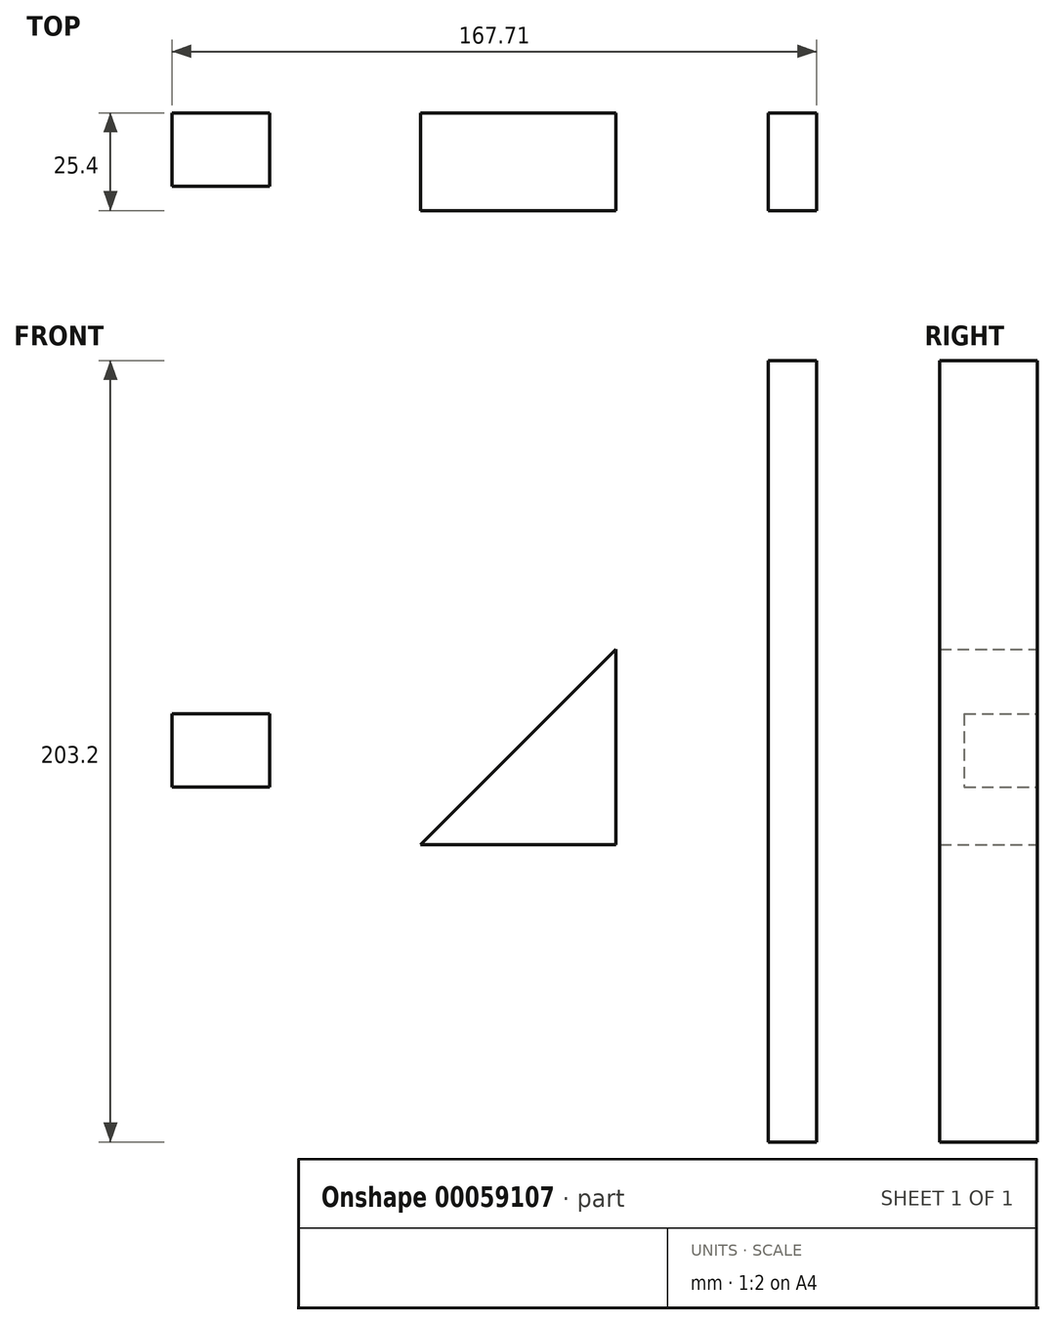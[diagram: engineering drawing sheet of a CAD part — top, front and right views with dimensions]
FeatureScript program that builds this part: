
annotation { "Feature Type Name" : "Feature", "Feature Type Description" : "" }
export const myFeature = defineFeature(function(context is Context, id is Id, definition is map)
    precondition{}
    {
        {
            var Q0;
            Q0=qCreatedBy(makeId("Front.planeOp"),FACE);
            var sketch = newSketch(context, id + "F0", { "sketchPlane" : qUnion([Q0])});
            skLineSegment(sketch, "E0.rect.bottom", {"start": v(6.35, -101.6) * mm, "end": v(-6.35, -101.6) * mm});
            skLineSegment(sketch, "E0.rect.top", {"start": v(6.35, 101.6) * mm, "end": v(-6.35, 101.6) * mm});
            skLineSegment(sketch, "E0.rect.left", {"start": v(6.35, -101.6) * mm, "end": v(6.35, 101.6) * mm});
            skLineSegment(sketch, "E0.rect.right", {"start": v(-6.35, -101.6) * mm, "end": v(-6.35, 101.6) * mm});
            skPoint(sketch, "E0.rect.middle", {"position": v(0, 0) * mm});
            skSolve(sketch);
        }
        {
            var Q0;
            Q0=makeQuery(id+"F0.imprint","IMPRINT",FACE,{"disambiguationData":[TD([[makeQuery(id+"F0.imprint","IMPRINT",EDGE,{"derivedFrom":sQuery(id+"F0.wireOp",EDGE,"E0.rect.bottom")}),-1.0]])]});
            extrude(context, id + "F1", {"entities" : qUnion([Q0]), "depth" : 25.4 * mm});
        }
        {
            var Q0;
            Q0=qCreatedBy(makeId("Front.planeOp"),FACE);
            var sketch = newSketch(context, id + "F2", { "sketchPlane" : qUnion([Q0])});
            skLineSegment(sketch, "E1.top", {"start": v(-96.76, -24.34) * mm, "end": v(-45.96, -24.34) * mm});
            skLineSegment(sketch, "E1.right", {"start": v(-45.96, 26.46) * mm, "end": v(-45.96, -24.34) * mm});
            skLineSegment(sketch, "E2", {"start": v(-96.76, -24.34) * mm, "end": v(-45.96, 26.46) * mm});
            skSolve(sketch);
        }
        {
            var Q0;
            Q0=makeQuery(id+"F2.imprint","IMPRINT",FACE,{"disambiguationData":[TD([[makeQuery(id+"F2.imprint","IMPRINT",EDGE,{"derivedFrom":sQuery(id+"F2.wireOp",EDGE,"E1.top")}),1.0]])]});
            extrude(context, id + "F3", {"entities" : qUnion([Q0]), "depth" : 25.4 * mm});
        }
        {
            var Q0;
            Q0=qCreatedBy(makeId("Front.planeOp"),FACE);
            var sketch = newSketch(context, id + "F4", { "sketchPlane" : qUnion([Q0])});
            skLineSegment(sketch, "E3.bottom", {"start": v(-161.36, 9.74) * mm, "end": v(-135.96, 9.74) * mm});
            skLineSegment(sketch, "E3.top", {"start": v(-161.36, -9.31) * mm, "end": v(-135.96, -9.31) * mm});
            skLineSegment(sketch, "E3.left", {"start": v(-161.36, 9.74) * mm, "end": v(-161.36, -9.31) * mm});
            skLineSegment(sketch, "E3.right", {"start": v(-135.96, 9.74) * mm, "end": v(-135.96, -9.31) * mm});
            skSolve(sketch);
        }
        {
            var Q0;
            Q0=makeQuery(id+"F4.imprint","IMPRINT",FACE,{"disambiguationData":[TD([[makeQuery(id+"F4.imprint","IMPRINT",EDGE,{"derivedFrom":sQuery(id+"F4.wireOp",EDGE,"E3.bottom")}),-1.0]])]});
            extrude(context, id + "F5", {"entities" : qUnion([Q0]), "depth" : 19.05 * mm});
        }
    });
